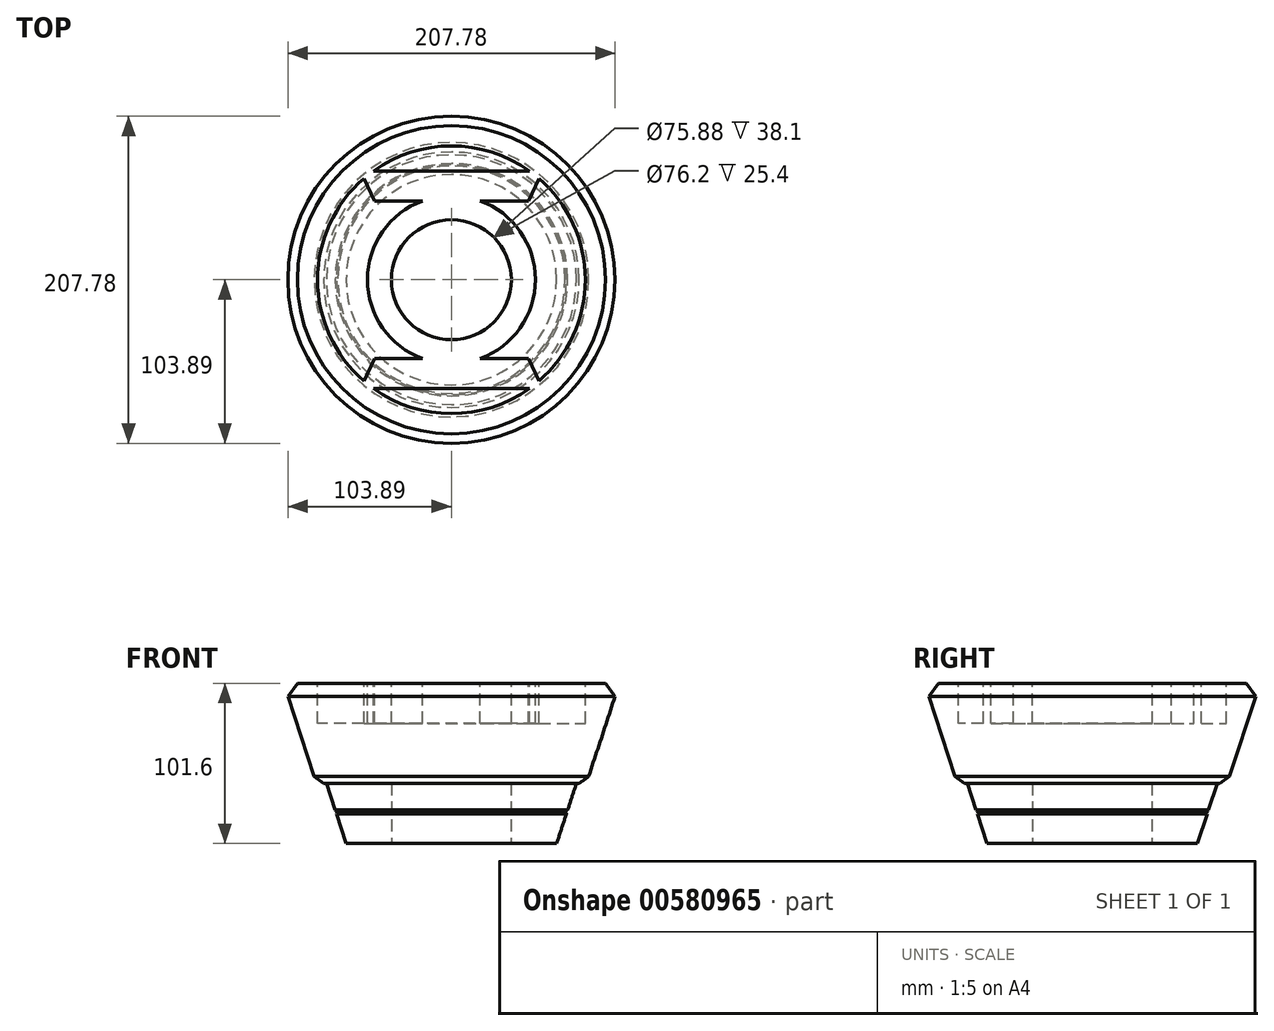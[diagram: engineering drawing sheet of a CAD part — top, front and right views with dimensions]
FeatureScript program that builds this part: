
annotation { "Feature Type Name" : "Feature", "Feature Type Description" : "" }
export const myFeature = defineFeature(function(context is Context, id is Id, definition is map)
    precondition{}
    {
        {
            var Q0;
            Q0=qCreatedBy(makeId("Top.planeOp"),FACE);
            var sketch = newSketch(context, id + "F0", { "sketchPlane" : qUnion([Q0])});
            skCircle(sketch, "E0", {"center": v(0, 0) * mm, "radius": 66.85 * mm});
            skSolve(sketch);
        }
        {
            var Q0;
            Q0=qCreatedBy(makeId("Top.planeOp"),FACE);
            cPlane(context, id + "F1", {"entities" : qUnion([Q0]), "cplaneType" : CPlaneType.OFFSET, "offset" : 101.6 * mm, "width" : 152.4 * mm, "height" : 152.4 * mm});
        }
        {
            var Q0;
            Q0=qCreatedBy(id+"F1.planeOp",FACE);
            var sketch = newSketch(context, id + "F2", { "sketchPlane" : qUnion([Q0])});
            skCircle(sketch, "E1", {"center": v(0, 0) * mm, "radius": 100.28 * mm});
            skSolve(sketch);
        }
        {
            var Q0;
            Q0=makeQuery(id+"F2.imprint","IMPRINT",FACE,{"disambiguationData":[TD([[makeQuery(id+"F2.imprint","IMPRINT",EDGE,{"derivedFrom":sQuery(id+"F2.wireOp",EDGE,"E1")}),1.0]])]});
            var Q1;
            Q1=makeQuery(id+"F0.imprint","IMPRINT",FACE,{"disambiguationData":[TD([[makeQuery(id+"F0.imprint","IMPRINT",EDGE,{"derivedFrom":sQuery(id+"F0.wireOp",EDGE,"E0")}),1.0]])]});
            var Q2;
            Q2=sQuery(id+"F2.wireOp",EDGE,"Eyu8YDiN-lEGU-Wuxt-0ncA-RZLAWeJK4OgB");
            var Q3;
            Q3=sQuery(id+"F0.wireOp",EDGE,"fgfE4CqQ-t5n6-ucAx-yhIW-5wF2yx0Jya2k");
            loft(context, id + "F3", {"sheetProfilesArray" : [{ "sheetProfileEntities" : qUnion([Q0]) }, { "sheetProfileEntities" : qUnion([Q1]) }], "wireProfilesArray" : [{ "wireProfileEntities" : qUnion([Q2]) }, { "wireProfileEntities" : qUnion([Q3]) }]});
        }
        {
            var Q0;
            Q0=qCreatedBy(makeId("Top.planeOp"),FACE);
            var sketch = newSketch(context, id + "F4", { "sketchPlane" : qUnion([Q0])});
            skCircle(sketch, "E2", {"center": v(0, 0) * mm, "radius": 37.94 * mm});
            skSolve(sketch);
        }
        {
            var Q0;
            Q0=makeQuery(id+"F4.imprint","IMPRINT",FACE,{"disambiguationData":[TD([[makeQuery(id+"F4.imprint","IMPRINT",EDGE,{"derivedFrom":sQuery(id+"F4.wireOp",EDGE,"E2")}),1.0]])]});
            extrude(context, id + "F5", {"entities" : qUnion([Q0]), "operationType" : NewBodyOperationType.REMOVE, "depth" : 53.34 * mm, "offsetDistance" : 25.4 * mm});
        }
        {
            var Q0;
            Q0=qCreatedBy(makeId("Top.planeOp"),FACE);
            cPlane(context, id + "F6", {"entities" : qUnion([Q0]), "cplaneType" : CPlaneType.OFFSET, "offset" : 38.1 * mm, "width" : 152.4 * mm, "height" : 152.4 * mm});
        }
        {
            var Q0;
            Q0=qCreatedBy(id+"F6.planeOp",FACE);
            var sketch = newSketch(context, id + "F7", { "sketchPlane" : qUnion([Q0])});
            skCircle(sketch, "E3", {"center": v(0, 0) * mm, "radius": 85.73 * mm});
            skSolve(sketch);
        }
        {
            var Q0;
            Q0=qCreatedBy(id+"F1.planeOp",FACE);
            var sketch = newSketch(context, id + "F8", { "sketchPlane" : qUnion([Q0])});
            skCircle(sketch, "E4", {"center": v(0, 0) * mm, "radius": 106.63 * mm});
            skSolve(sketch);
        }
        {
            var Q1;
            Q1=makeQuery(id+"F7.imprint","IMPRINT",FACE,{"disambiguationData":[TD([[makeQuery(id+"F7.imprint","IMPRINT",EDGE,{"derivedFrom":sQuery(id+"F7.wireOp",EDGE,"E3")}),1.0]])]});
            var Q2;
            Q2=makeQuery(id+"F8.imprint","IMPRINT",FACE,{"disambiguationData":[TD([[makeQuery(id+"F8.imprint","IMPRINT",EDGE,{"derivedFrom":sQuery(id+"F8.wireOp",EDGE,"E4")}),1.0]])]});
            loft(context, id + "F9", {"operationType" : NewBodyOperationType.ADD, "sheetProfilesArray" : [{ "sheetProfileEntities" : qUnion([Q1]) }, { "sheetProfileEntities" : qUnion([Q2]) }]});
        }
        {
            var Q0;
            Q0=makeQuery(id+"F9.opLoft","MID_CAP_EDGE",EDGE,{"disambiguationData":[OSD([sQuery(id+"F7.wireOp",EDGE,"E3")])],"capPos":0.0});
            chamfer(context, id + "F10", {"entities" : qUnion([Q0]), "width" : 6.35 * mm, "tangentPropagation" : true});
        }
        {
            var Q0;
            Q0=makeQuery(id+"F9.opLoft","MID_CAP_EDGE",EDGE,{"disambiguationData":[OSD([sQuery(id+"F7.wireOp",EDGE,"E3"),sQuery(id+"F8.wireOp",EDGE,"E4")])],"capPos":1.0});
            chamfer(context, id + "F11", {"entities" : qUnion([Q0]), "width" : 6.35 * mm, "tangentPropagation" : true});
        }
        {
            var Q0;
            Q0=qCreatedBy(makeId("Front.planeOp"),FACE);
            var sketch = newSketch(context, id + "F12", { "sketchPlane" : qUnion([Q0])});
            skLineSegment(sketch, "E5", {"start": v(-79.4, 38.11) * mm, "end": v(-66.85, 0) * mm});
            skLineSegment(sketch, "E6", {"start": v(-73.8, 21.14) * mm, "end": v(-72.2, 20.33) * mm});
            skLineSegment(sketch, "E7", {"start": v(-72.2, 20.33) * mm, "end": v(-73.02, 18.73) * mm});
            skSolve(sketch);
        }
        {
            var Q0;
            Q0=qCreatedBy(makeId("Right.planeOp"),FACE);
            var sketch = newSketch(context, id + "F13", { "sketchPlane" : qUnion([Q0])});
            skLineSegment(sketch, "E8", {"start": v(0, 0) * mm, "end": v(0, 184.2) * mm});
            skSolve(sketch);
        }
        {
            var Q0;
            Q0=qSketchRegion(id+"F12",true);
            var Q1;
            Q1=sQuery(id+"F13.wireOp",EDGE,"E8");
            revolve(context, id + "F14", {"operationType" : NewBodyOperationType.REMOVE, "entities" : qUnion([Q0]), "axis" : qUnion([Q1]), "revolveType" : RevolveType.FULL, "oppositeDirection" : true});
        }
        {
            var Q0;
            Q0=makeQuery(id+"F9.boolean.opBoolean","MERGE",FACE,{"derivedFrom":[makeQuery(id+"F3.opLoft","CAP_FACE",FACE,{"disambiguationData":[OSD([makeQuery(id+"F2.imprint","IMPRINT",FACE,{"disambiguationData":[TD([[makeQuery(id+"F2.imprint","IMPRINT",EDGE,{"derivedFrom":sQuery(id+"F2.wireOp",EDGE,"E1")}),1.0]])]})])],"isStart":true}),makeQuery(id+"F9.opLoft","CAP_FACE",FACE,{"disambiguationData":[OSD([makeQuery(id+"F8.imprint","IMPRINT",FACE,{"disambiguationData":[TD([[makeQuery(id+"F8.imprint","IMPRINT",EDGE,{"derivedFrom":sQuery(id+"F8.wireOp",EDGE,"E4")}),1.0]])]})])],"isStart":true})]});
            var sketch = newSketch(context, id + "F15", { "sketchPlane" : qUnion([Q0])});
            skCircle(sketch, "E9", {"center": v(0, 0) * mm, "radius": 38.1 * mm});
            skArc(sketch, "E10", {"start": v(18.28, -50.1) * mm, "mid": v(53.34, 0) * mm, "end": v(18.28, 50.1) * mm});
            skLineSegment(sketch, "E11", {"start": v(-57.78, 69.16) * mm, "end": v(57.78, 69.16) * mm});
            skLineSegment(sketch, "E12", {"start": v(-48.9, 50.1) * mm, "end": v(-18.28, 50.1) * mm});
            skLineSegment(sketch, "E13", {"start": v(-57.78, 69.16) * mm, "end": v(-48.9, 50.1) * mm});
            skLineSegment(sketch, "E14", {"start": v(48.9, 50.1) * mm, "end": v(57.78, 69.16) * mm});
            skLineSegment(sketch, "E15", {"start": v(-48.9, 50.1) * mm, "end": v(-48.9, 55.17) * mm});
            skLineSegment(sketch, "E16", {"start": v(48.9, 50.1) * mm, "end": v(48.9, 55.17) * mm});
            skLineSegment(sketch, "E17", {"start": v(-53.34, 59.63) * mm, "end": v(-53.34, 42.82) * mm});
            skLineSegment(sketch, "E18", {"start": v(0, 0) * mm, "end": v(23.58, 0) * mm});
            skLineSegment(sketch, "E19.MirrorCS", {"start": v(48.9, -50.1) * mm, "end": v(57.78, -69.16) * mm});
            skLineSegment(sketch, "E20.MirrorCS", {"start": v(-48.9, -50.1) * mm, "end": v(-18.28, -50.1) * mm});
            skLineSegment(sketch, "E21.MirrorCS", {"start": v(-57.78, -69.16) * mm, "end": v(57.78, -69.16) * mm});
            skLineSegment(sketch, "E22.MirrorCS", {"start": v(-57.78, -69.16) * mm, "end": v(-48.9, -50.1) * mm});
            skArc(sketch, "E23.trimOffspring", {"start": v(-18.28, 50.1) * mm, "mid": v(-53.34, 0) * mm, "end": v(-18.28, -50.1) * mm});
            skLineSegment(sketch, "E24.trimOffspring", {"start": v(18.28, 50.1) * mm, "end": v(48.9, 50.1) * mm});
            skLineSegment(sketch, "E25.trimOffspring", {"start": v(18.28, -50.1) * mm, "end": v(48.9, -50.1) * mm});
            skCircle(sketch, "E26", {"center": v(0, 0) * mm, "radius": 100.28 * mm});
            skCircle(sketch, "E27", {"center": v(0, 0) * mm, "radius": 85.04 * mm});
            skSolve(sketch);
        }
        {
            var Q0;
            Q0=makeQuery(id+"F15.imprint","IMPRINT",FACE,{"disambiguationData":[TD([[makeQuery(id+"F15.imprint","IMPRINT",EDGE,{"derivedFrom":sQuery(id+"F15.wireOp",EDGE,"E9")}),1.0]])]});
            var Q1;
            {var subQ1=sQuery(id+"F15.wireOp",EDGE,"E12");Q1=makeQuery(id+"F15.imprint","IMPRINT",FACE,{"disambiguationData":[TD([[makeQuery(id+"F15.imprint","IMPRINT",EDGE,{"derivedFrom":subQ1}),-1.0]])]});}
            var Q2;
            Q2=makeQuery(id+"F15.imprint","IMPRINT",FACE,{"disambiguationData":[TD([[makeQuery(id+"F15.imprint","IMPRINT",EDGE,{"derivedFrom":sQuery(id+"F15.wireOp",EDGE,"E10")}),-1.0]])]});
            var Q3;
            {var subQ0=sQuery(id+"F15.wireOp",EDGE,"E11");Q3=makeQuery(id+"F15.imprint","IMPRINT",FACE,{"disambiguationData":[TD([[makeQuery(id+"F15.imprint","IMPRINT",EDGE,{"derivedFrom":subQ0}),1.0]])]});}
            var Q4;
            {var subQ0=sQuery(id+"F15.wireOp",EDGE,"E21.MirrorCS");Q4=makeQuery(id+"F15.imprint","IMPRINT",FACE,{"disambiguationData":[TD([[makeQuery(id+"F15.imprint","IMPRINT",EDGE,{"derivedFrom":subQ0}),-1.0]])]});}
            extrude(context, id + "F16", {"entities" : qUnion([Q0, Q1, Q2, Q3, Q4]), "operationType" : NewBodyOperationType.REMOVE, "oppositeDirection" : true, "depth" : 25.4 * mm, "offsetDistance" : 25.4 * mm});
        }
    });
